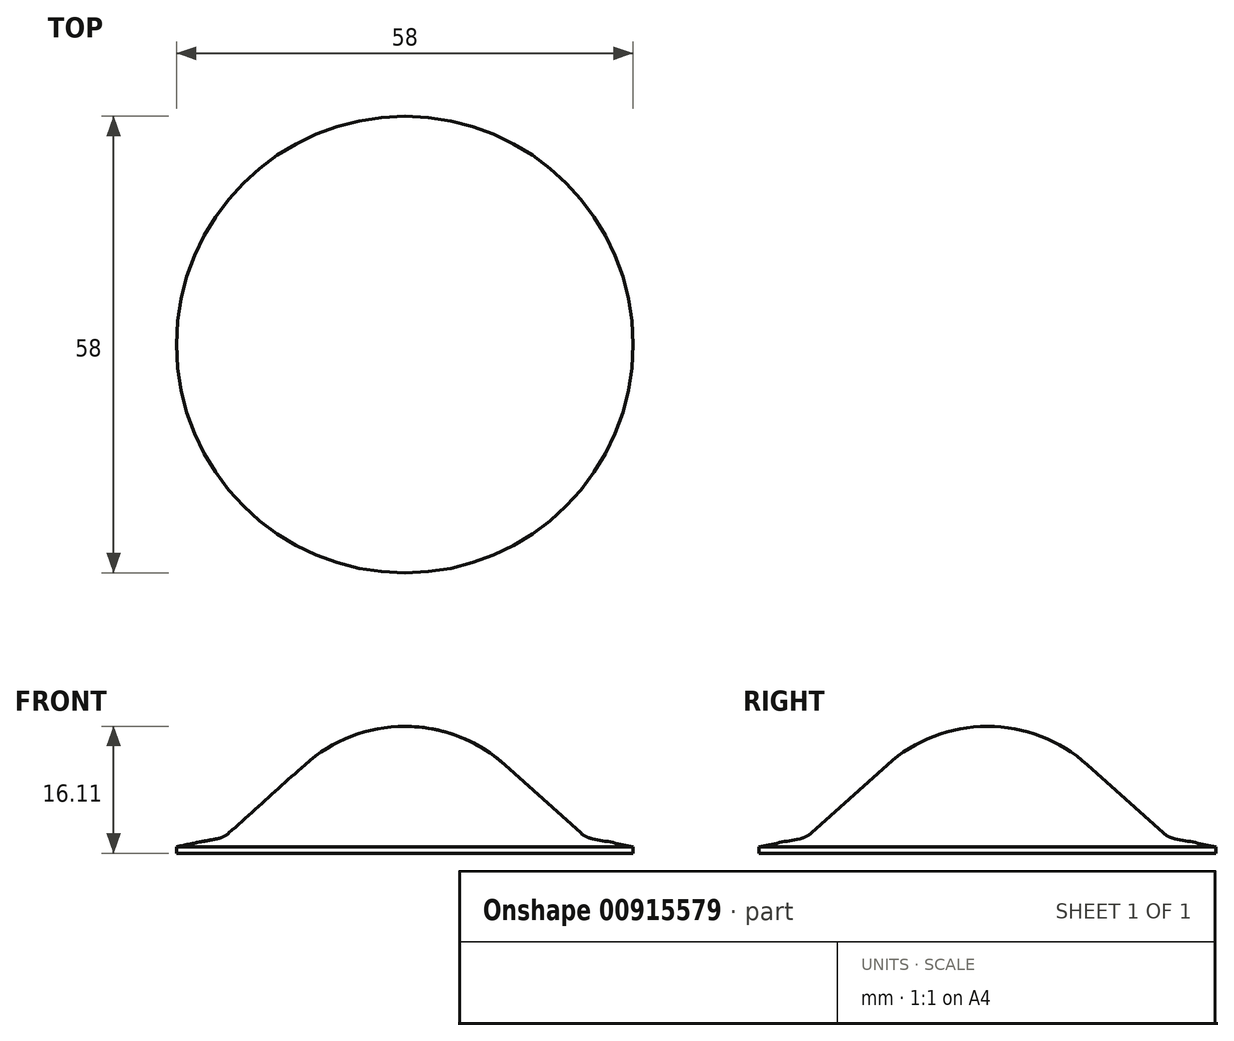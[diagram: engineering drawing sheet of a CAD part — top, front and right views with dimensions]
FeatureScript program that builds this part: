
annotation { "Feature Type Name" : "Feature", "Feature Type Description" : "" }
export const myFeature = defineFeature(function(context is Context, id is Id, definition is map)
    precondition{}
    {
        {
            var Q0;
            Q0=qCreatedBy(makeId("Front.planeOp"),FACE);
            var sketch = newSketch(context, id + "F0", { "sketchPlane" : qUnion([Q0])});
            skLineSegment(sketch, "E0.bottom", {"start": v(29, -0.4) * mm, "end": v(-29, -0.4) * mm});
            skLineSegment(sketch, "E0.top", {"start": v(29, 0.4) * mm, "end": v(-29, 0.4) * mm});
            skLineSegment(sketch, "E0.left", {"start": v(29, -0.4) * mm, "end": v(29, 0.4) * mm});
            skLineSegment(sketch, "E0.right", {"start": v(-29, -0.4) * mm, "end": v(-29, 0.4) * mm});
            skPoint(sketch, "E0.middle", {"position": v(0, 0) * mm});
            skArc(sketch, "E1", {"start": v(-23.84, 1.43) * mm, "mid": v(-26.42, 0.94) * mm, "end": v(-29, 0.4) * mm});
            skCircle(sketch, "E2", {"center": v(0, -3.3) * mm, "radius": 19 * mm});
            skLineSegment(sketch, "E3", {"start": v(-12.7, 10.84) * mm, "end": v(-22.36, 2.15) * mm});
            skLineSegment(sketch, "E4", {"start": v(12.7, 10.84) * mm, "end": v(23, 1.58) * mm});
            skLineSegment(sketch, "E5", {"start": v(0, 0) * mm, "end": v(0, 20.81) * mm});
            skPoint(sketch, "E5.endSnap0", {"position": v(0, 3.55) * mm});
            skArc(sketch, "E6.filletArc", {"start": v(-23.84, 1.43) * mm, "mid": v(-23.05, 1.69) * mm, "end": v(-22.36, 2.15) * mm});
            skLineSegment(sketch, "E7", {"start": v(0, 0) * mm, "end": v(0, -3.3) * mm});
            skSolve(sketch);
        }
        {
            var Q0;
            {var subQ1=sQuery(id+"F0.wireOp",EDGE,"E1");Q0=makeQuery(id+"F0.imprint","IMPRINT",FACE,{"disambiguationData":[TD([[makeQuery(id+"F0.imprint","IMPRINT",EDGE,{"derivedFrom":subQ1}),1.0]])]});}
            var Q1;
            {var subQ0=sQuery(id+"F0.wireOp",EDGE,"E5");var subQ1=sQuery(id+"F0.wireOp",EDGE,"E0.top");var subQ2=makeQuery(id+"F0.imprint","INTERSECT",VERTEX,{"derivedFrom":[subQ1,subQ0]});Q1=makeQuery(id+"F0.imprint","IMPRINT",FACE,{"disambiguationData":[TD([[makeQuery(id+"F0.imprint","IMPRINT",EDGE,{"disambiguationData":[TD([[subQ2,-1.0]])],"derivedFrom":subQ1}),-1.0]])]});}
            var Q2;
            {var subQ0=sQuery(id+"F0.wireOp",EDGE,"E7");var subQ6=sQuery(id+"F0.wireOp",EDGE,"E0.bottom");var subQ9=makeQuery(id+"F0.imprint","INTERSECT",VERTEX,{"derivedFrom":[subQ6,subQ0]});Q2=makeQuery(id+"F0.imprint","IMPRINT",FACE,{"disambiguationData":[TD([[makeQuery(id+"F0.imprint","IMPRINT",EDGE,{"disambiguationData":[TD([[subQ9,-1.0]])],"derivedFrom":subQ6}),-1.0]])]});}
            var Q3;
            {var subQ0=sQuery(id+"F0.wireOp",EDGE,"E0.right");Q3=makeQuery(id+"F0.imprint","IMPRINT",FACE,{"disambiguationData":[TD([[makeQuery(id+"F0.imprint","IMPRINT",EDGE,{"derivedFrom":subQ0}),-1.0]])]});}
            var Q4;
            Q4=sQuery(id+"F0.wireOp",EDGE,"E5");
            revolve(context, id + "F1", {"surfaceOperationType" : NewSurfaceOperationType.NEW, "entities" : qUnion([Q0, Q1, Q2, Q3]), "axis" : qUnion([Q4]), "revolveType" : RevolveType.FULL});
        }
    });
